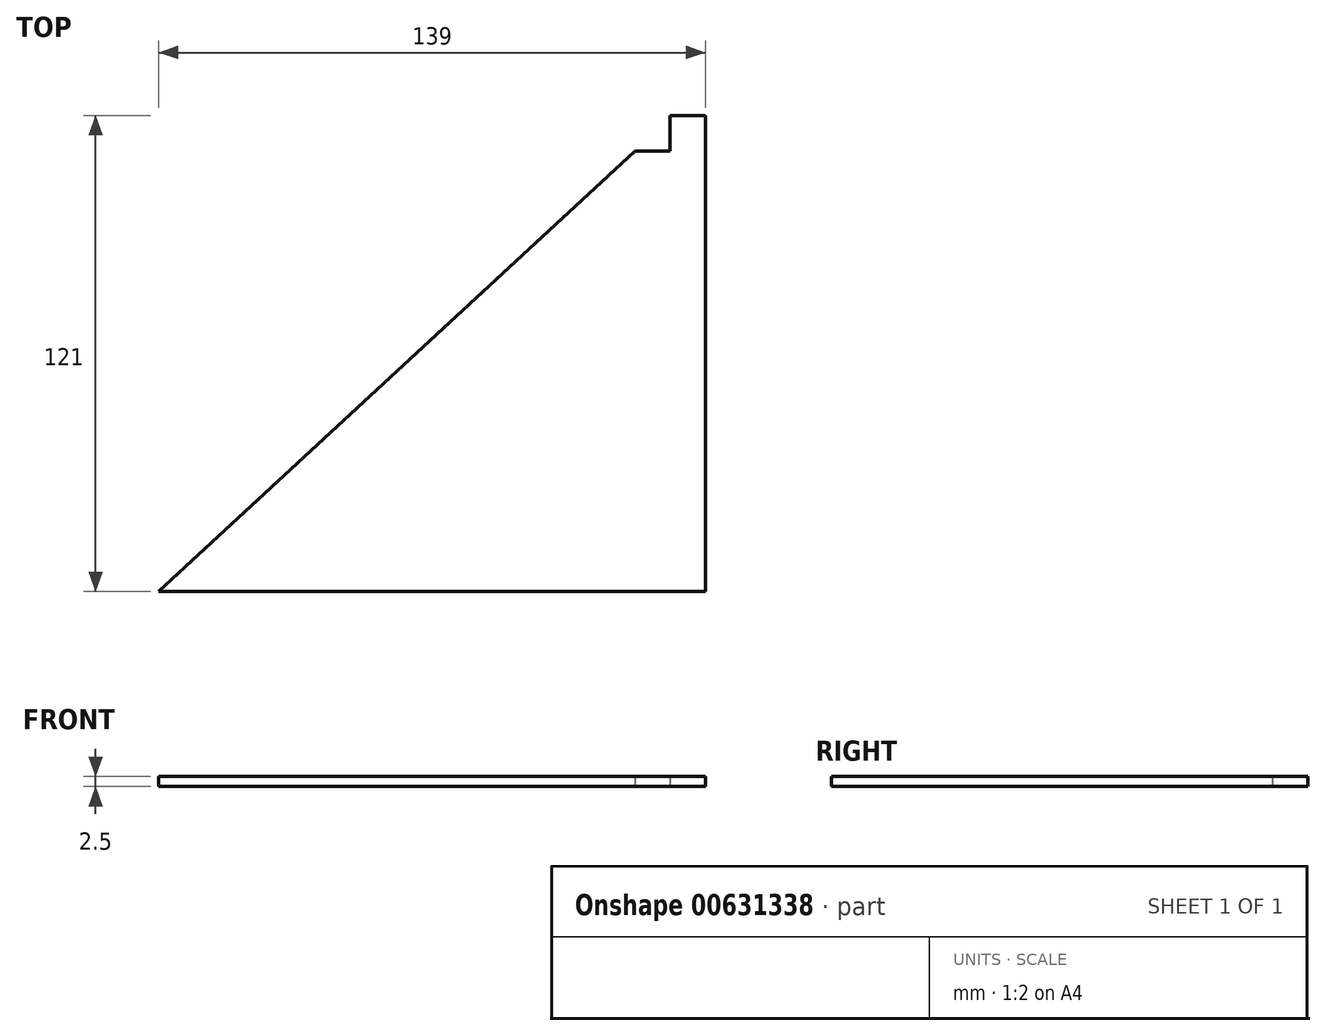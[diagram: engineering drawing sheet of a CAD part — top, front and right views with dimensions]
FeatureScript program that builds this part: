
annotation { "Feature Type Name" : "Feature", "Feature Type Description" : "" }
export const myFeature = defineFeature(function(context is Context, id is Id, definition is map)
    precondition{}
    {
        {
            var Q0;
            Q0=qCreatedBy(makeId("Top.planeOp"),FACE);
            var sketch = newSketch(context, id + "F0", { "sketchPlane" : qUnion([Q0])});
            skLineSegment(sketch, "E0", {"start": v(70.73, -20.44) * mm, "end": v(-68.27, -20.44) * mm});
            skLineSegment(sketch, "E1", {"start": v(70.73, -20.44) * mm, "end": v(70.73, 100.56) * mm});
            skLineSegment(sketch, "E2", {"start": v(70.73, 91.56) * mm, "end": v(61.73, 91.56) * mm});
            skLineSegment(sketch, "E3", {"start": v(61.73, 91.56) * mm, "end": v(61.73, 100.56) * mm});
            skLineSegment(sketch, "E4", {"start": v(61.73, 91.56) * mm, "end": v(52.73, 91.56) * mm});
            skLineSegment(sketch, "E5", {"start": v(52.73, 91.56) * mm, "end": v(-68.27, -20.44) * mm});
            skLineSegment(sketch, "E6", {"start": v(61.73, 100.56) * mm, "end": v(70.73, 100.56) * mm});
            skLineSegment(sketch, "E7.bottom", {"start": v(-68.27, -20.44) * mm, "end": v(-59.27, -20.44) * mm});
            skLineSegment(sketch, "E7.top", {"start": v(-68.27, -29.44) * mm, "end": v(-59.27, -29.44) * mm});
            skLineSegment(sketch, "E7.left", {"start": v(-68.27, -20.44) * mm, "end": v(-68.27, -29.44) * mm});
            skLineSegment(sketch, "E7.right", {"start": v(-59.27, -20.44) * mm, "end": v(-59.27, -29.44) * mm});
            skLineSegment(sketch, "E8.bottom", {"start": v(-50.27, -20.44) * mm, "end": v(52.73, -20.44) * mm});
            skLineSegment(sketch, "E8.top", {"start": v(-50.27, -29.44) * mm, "end": v(52.73, -29.44) * mm});
            skLineSegment(sketch, "E8.left", {"start": v(-50.27, -20.44) * mm, "end": v(-50.27, -29.44) * mm});
            skLineSegment(sketch, "E8.right", {"start": v(52.73, -20.44) * mm, "end": v(52.73, -29.44) * mm});
            skLineSegment(sketch, "E9.bottom", {"start": v(70.73, -20.44) * mm, "end": v(61.73, -20.44) * mm});
            skLineSegment(sketch, "E9.top", {"start": v(70.73, -29.44) * mm, "end": v(61.73, -29.44) * mm});
            skLineSegment(sketch, "E9.left", {"start": v(70.73, -20.44) * mm, "end": v(70.73, -29.44) * mm});
            skLineSegment(sketch, "E9.right", {"start": v(61.73, -20.44) * mm, "end": v(61.73, -29.44) * mm});
            skSolve(sketch);
        }
        {
            var Q0;
            {var subQ2=sQuery(id+"F0.wireOp",EDGE,"E0");Q0=makeQuery(id+"F0.imprint","IMPRINT",FACE,{"disambiguationData":[TD([[makeQuery(id+"F0.imprint","IMPRINT",EDGE,{"derivedFrom":subQ2}),-1.0]])]});}
            var Q1;
            {var subQ2=sQuery(id+"F0.wireOp",EDGE,"E2");Q1=makeQuery(id+"F0.imprint","IMPRINT",FACE,{"disambiguationData":[TD([[makeQuery(id+"F0.imprint","IMPRINT",EDGE,{"derivedFrom":subQ2}),-1.0]])]});}
            var Q2;
            Q2=makeQuery(id+"F0.imprint","IMPRINT",FACE,{"disambiguationData":[TD([[makeQuery(id+"F0.imprint","IMPRINT",EDGE,{"derivedFrom":sQuery(id+"F0.wireOp",EDGE,"E7.bottom")}),-1.0]])]});
            var Q3;
            Q3=makeQuery(id+"F0.imprint","IMPRINT",FACE,{"disambiguationData":[TD([[makeQuery(id+"F0.imprint","IMPRINT",EDGE,{"derivedFrom":sQuery(id+"F0.wireOp",EDGE,"E8.bottom")}),-1.0]])]});
            var Q4;
            Q4=makeQuery(id+"F0.imprint","IMPRINT",FACE,{"disambiguationData":[TD([[makeQuery(id+"F0.imprint","IMPRINT",EDGE,{"derivedFrom":sQuery(id+"F0.wireOp",EDGE,"E9.bottom")}),1.0]])]});
            extrude(context, id + "F1", {"entities" : qUnion([Q0, Q1, Q2, Q3, Q4]), "depth" : 2.5 * mm, "offsetDistance" : 25 * mm});
        }
    });
